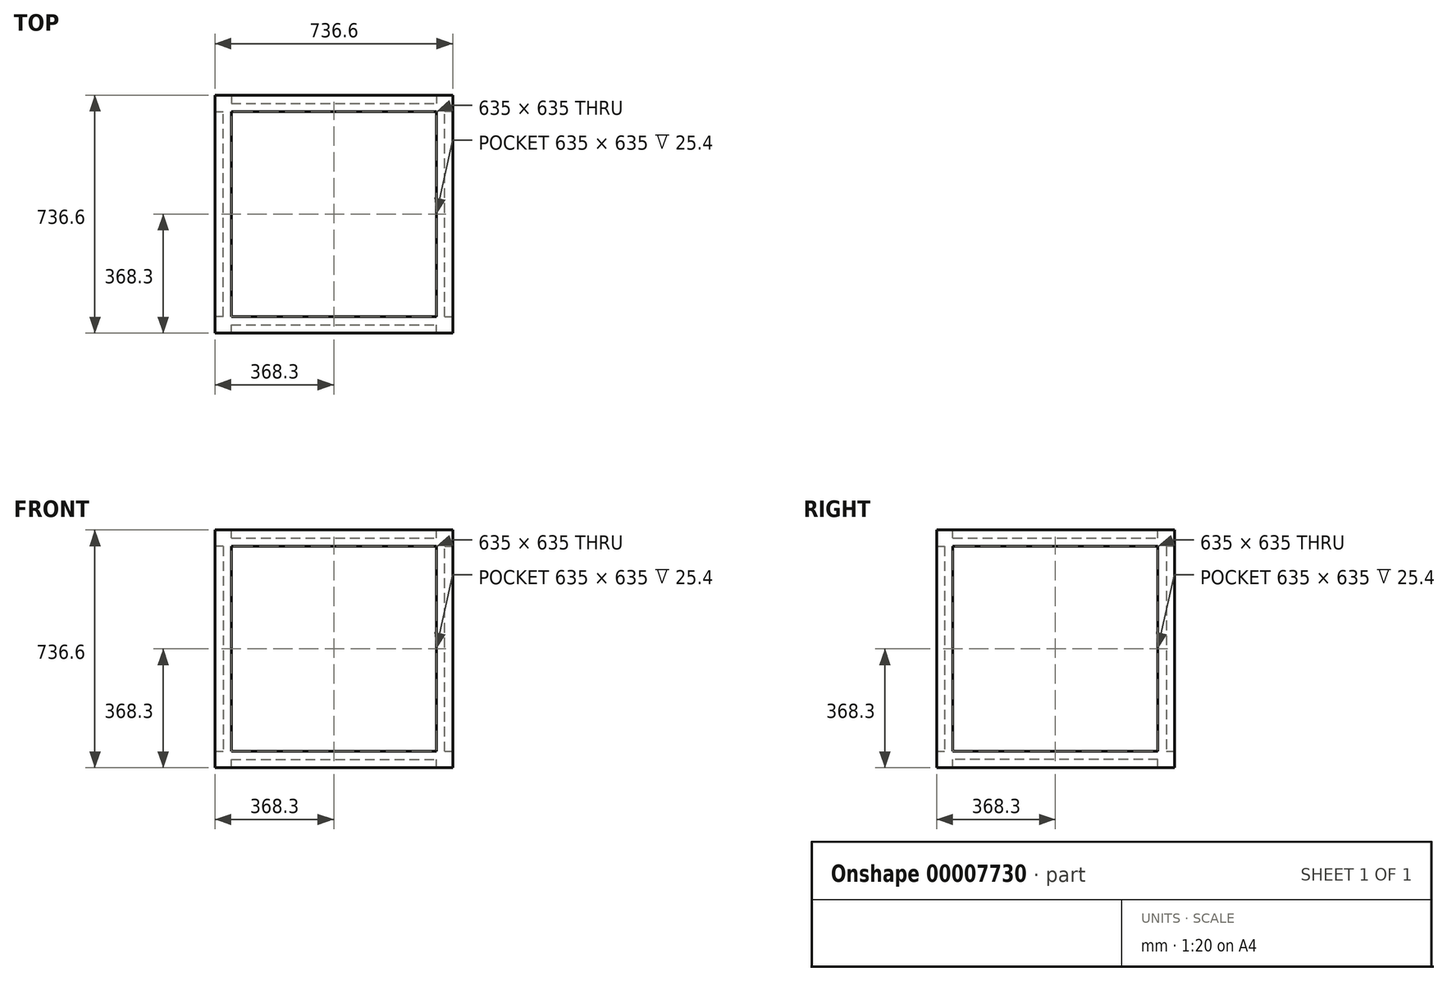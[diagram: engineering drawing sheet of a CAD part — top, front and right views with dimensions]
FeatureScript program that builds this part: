
annotation { "Feature Type Name" : "Feature", "Feature Type Description" : "" }
export const myFeature = defineFeature(function(context is Context, id is Id, definition is map)
    precondition{}
    {
        {
            var Q0;
            Q0=qCreatedBy(makeId("Front.planeOp"),FACE);
            var sketch = newSketch(context, id + "F0", { "sketchPlane" : qUnion([Q0])});
            skLineSegment(sketch, "E0.bottom", {"start": v(0, 0) * mm, "end": v(685.8, 0) * mm});
            skLineSegment(sketch, "E0.top", {"start": v(0, 685.8) * mm, "end": v(685.8, 685.8) * mm});
            skLineSegment(sketch, "E0.left", {"start": v(0, 0) * mm, "end": v(0, 685.8) * mm});
            skLineSegment(sketch, "E0.right", {"start": v(685.8, 0) * mm, "end": v(685.8, 685.8) * mm});
            skSolve(sketch);
        }
        {
            var Q0;
            Q0=makeQuery(id+"F0.imprint","IMPRINT",FACE,{"disambiguationData":[TD([[makeQuery(id+"F0.imprint","IMPRINT",EDGE,{"derivedFrom":sQuery(id+"F0.wireOp",EDGE,"E0.bottom")}),1.0]])]});
            extrude(context, id + "F1", {"entities" : qUnion([Q0]), "depth" : 685.8 * mm});
        }
        {
            var Q0;
            Q0=makeQuery(id+"F1.opExtrude","SWEPT_FACE",FACE,{"disambiguationData":[OSD([sQuery(id+"F0.wireOp",EDGE,"E0.right")])]});
            var sketch = newSketch(context, id + "F2", { "sketchPlane" : qUnion([Q0])});
            skLineSegment(sketch, "E1.0", {"start": v(-685.8, 0) * mm, "end": v(-685.8, 685.8) * mm, "construction": true});
            skLineSegment(sketch, "E2.0", {"start": v(0, 0) * mm, "end": v(0, 685.8) * mm, "construction": true});
            skLineSegment(sketch, "E3.0", {"start": v(-685.8, 685.8) * mm, "end": v(0, 685.8) * mm, "construction": true});
            skLineSegment(sketch, "E4.rect.bottom", {"start": v(-711.2, 711.2) * mm, "end": v(-660.4, 711.2) * mm});
            skLineSegment(sketch, "E4.rect.top", {"start": v(-711.2, 660.4) * mm, "end": v(-685.8, 660.4) * mm});
            skLineSegment(sketch, "E4.rect.left", {"start": v(-711.2, 711.2) * mm, "end": v(-711.2, 660.4) * mm});
            skLineSegment(sketch, "E4.rect.right", {"start": v(-660.4, 711.2) * mm, "end": v(-660.4, 685.8) * mm});
            skPoint(sketch, "E4.rect.middle", {"position": v(-685.8, 685.8) * mm});
            skPoint(sketch, "E5.orphan", {"position": v(-660.4, 660.4) * mm});
            skLineSegment(sketch, "E6", {"start": v(-660.4, 685.8) * mm, "end": v(-685.8, 685.8) * mm});
            skLineSegment(sketch, "E7", {"start": v(-685.8, 660.4) * mm, "end": v(-685.8, 685.8) * mm});
            skLineSegment(sketch, "E8.rect.bottom", {"start": v(25.4, 711.2) * mm, "end": v(-25.4, 711.2) * mm});
            skLineSegment(sketch, "E8.rect.top", {"start": v(25.4, 660.4) * mm, "end": v(0, 660.4) * mm});
            skLineSegment(sketch, "E8.rect.left", {"start": v(25.4, 711.2) * mm, "end": v(25.4, 660.4) * mm});
            skLineSegment(sketch, "E8.rect.right", {"start": v(-25.4, 711.2) * mm, "end": v(-25.4, 685.8) * mm});
            skPoint(sketch, "E8.rect.middle", {"position": v(0, 685.8) * mm});
            skLineSegment(sketch, "E9.rect.bottom", {"start": v(0, 25.4) * mm, "end": v(25.4, 25.4) * mm});
            skLineSegment(sketch, "E9.rect.top", {"start": v(-25.4, -25.4) * mm, "end": v(25.4, -25.4) * mm});
            skLineSegment(sketch, "E9.rect.right", {"start": v(25.4, 25.4) * mm, "end": v(25.4, -25.4) * mm});
            skPoint(sketch, "E9.rect.middle", {"position": v(0, 0) * mm});
            skLineSegment(sketch, "E10.rect.bottom", {"start": v(-711.2, -25.4) * mm, "end": v(-660.4, -25.4) * mm});
            skLineSegment(sketch, "E10.rect.top", {"start": v(-711.2, 25.4) * mm, "end": v(-685.8, 25.4) * mm});
            skLineSegment(sketch, "E10.rect.left", {"start": v(-711.2, -25.4) * mm, "end": v(-711.2, 25.4) * mm});
            skPoint(sketch, "E10.rect.middle", {"position": v(-685.8, 0) * mm});
            skPoint(sketch, "E11.orphan", {"position": v(-25.4, 660.4) * mm});
            skPoint(sketch, "E12.orphan", {"position": v(-660.4, 25.4) * mm});
            skPoint(sketch, "E13.orphan", {"position": v(-25.4, 25.4) * mm});
            skLineSegment(sketch, "E14", {"start": v(-25.4, 685.8) * mm, "end": v(0, 685.8) * mm});
            skLineSegment(sketch, "E15", {"start": v(0, 685.8) * mm, "end": v(0, 660.4) * mm});
            skLineSegment(sketch, "E16", {"start": v(0, 25.4) * mm, "end": v(0, 0) * mm});
            skLineSegment(sketch, "E17", {"start": v(-25.4, -25.4) * mm, "end": v(-25.4, 0) * mm});
            skLineSegment(sketch, "E18", {"start": v(-25.4, 0) * mm, "end": v(0, 0) * mm});
            skLineSegment(sketch, "E19", {"start": v(-660.4, -25.4) * mm, "end": v(-660.4, 0) * mm});
            skLineSegment(sketch, "E20", {"start": v(-660.4, 0) * mm, "end": v(-685.8, 0) * mm});
            skLineSegment(sketch, "E21", {"start": v(-685.8, 25.4) * mm, "end": v(-685.8, 0) * mm});
            skSolve(sketch);
        }
        {
            var Q0;
            Q0=makeQuery(id+"F2.imprint","IMPRINT",FACE,{"disambiguationData":[TD([[makeQuery(id+"F2.imprint","IMPRINT",EDGE,{"derivedFrom":sQuery(id+"F2.wireOp",EDGE,"E4.rect.bottom")}),-1.0]])]});
            var Q1;
            Q1=makeQuery(id+"F2.imprint","IMPRINT",FACE,{"disambiguationData":[TD([[makeQuery(id+"F2.imprint","IMPRINT",EDGE,{"derivedFrom":sQuery(id+"F2.wireOp",EDGE,"E8.rect.bottom")}),1.0]])]});
            var Q2;
            Q2=makeQuery(id+"F2.imprint","IMPRINT",FACE,{"disambiguationData":[TD([[makeQuery(id+"F2.imprint","IMPRINT",EDGE,{"derivedFrom":sQuery(id+"F2.wireOp",EDGE,"E9.rect.bottom")}),-1.0]])]});
            var Q3;
            Q3=makeQuery(id+"F2.imprint","IMPRINT",FACE,{"disambiguationData":[TD([[makeQuery(id+"F2.imprint","IMPRINT",EDGE,{"derivedFrom":sQuery(id+"F2.wireOp",EDGE,"E10.rect.bottom")}),1.0]])]});
            extrude(context, id + "F3", {"entities" : qUnion([Q0, Q1, Q2, Q3]), "operationType" : NewBodyOperationType.ADD, "oppositeDirection" : true, "depth" : 685.8 * mm});
        }
        {
            var Q0;
            Q0=makeQuery(id+"F1.opExtrude","CAP_FACE",FACE,{"disambiguationData":[OSD([sQuery(id+"F0.wireOp",EDGE,"E0.bottom"),sQuery(id+"F0.wireOp",EDGE,"E0.top"),sQuery(id+"F0.wireOp",EDGE,"E0.left"),sQuery(id+"F0.wireOp",EDGE,"E0.right")])],"isStart":true});
            var sketch = newSketch(context, id + "F4", { "sketchPlane" : qUnion([Q0])});
            skPoint(sketch, "E22.0", {"position": v(0, 685.8) * mm});
            skPoint(sketch, "E23.0", {"position": v(0, 0) * mm});
            skPoint(sketch, "E24.0", {"position": v(-685.8, 685.8) * mm});
            skPoint(sketch, "E25.0", {"position": v(-685.8, 0) * mm});
            skLineSegment(sketch, "E26.0", {"start": v(0, 711.2) * mm, "end": v(-685.8, 711.2) * mm, "construction": true});
            skLineSegment(sketch, "E27.0", {"start": v(0, -25.4) * mm, "end": v(-685.8, -25.4) * mm, "construction": true});
            skLineSegment(sketch, "E28.rect.bottom", {"start": v(-25.4, 711.2) * mm, "end": v(25.4, 711.2) * mm});
            skLineSegment(sketch, "E28.rect.top", {"start": v(-25.4, 660.4) * mm, "end": v(25.4, 660.4) * mm});
            skLineSegment(sketch, "E28.rect.left", {"start": v(-25.4, 711.2) * mm, "end": v(-25.4, 660.4) * mm});
            skLineSegment(sketch, "E28.rect.right", {"start": v(25.4, 711.2) * mm, "end": v(25.4, 660.4) * mm});
            skLineSegment(sketch, "E29.rect.bottom", {"start": v(-660.4, 711.2) * mm, "end": v(-711.2, 711.2) * mm});
            skLineSegment(sketch, "E29.rect.top", {"start": v(-660.4, 660.4) * mm, "end": v(-711.2, 660.4) * mm});
            skLineSegment(sketch, "E29.rect.left", {"start": v(-660.4, 711.2) * mm, "end": v(-660.4, 660.4) * mm});
            skLineSegment(sketch, "E29.rect.right", {"start": v(-711.2, 711.2) * mm, "end": v(-711.2, 660.4) * mm});
            skLineSegment(sketch, "E30.rect.bottom", {"start": v(-25.4, -25.4) * mm, "end": v(25.4, -25.4) * mm});
            skLineSegment(sketch, "E30.rect.top", {"start": v(-25.4, 25.4) * mm, "end": v(25.4, 25.4) * mm});
            skLineSegment(sketch, "E30.rect.left", {"start": v(-25.4, -25.4) * mm, "end": v(-25.4, 25.4) * mm});
            skLineSegment(sketch, "E30.rect.right", {"start": v(25.4, -25.4) * mm, "end": v(25.4, 25.4) * mm});
            skLineSegment(sketch, "E31.rect.bottom", {"start": v(-660.4, -25.4) * mm, "end": v(-711.2, -25.4) * mm});
            skLineSegment(sketch, "E31.rect.top", {"start": v(-660.4, 25.4) * mm, "end": v(-711.2, 25.4) * mm});
            skLineSegment(sketch, "E31.rect.left", {"start": v(-660.4, -25.4) * mm, "end": v(-660.4, 25.4) * mm});
            skLineSegment(sketch, "E31.rect.right", {"start": v(-711.2, -25.4) * mm, "end": v(-711.2, 25.4) * mm});
            skSolve(sketch);
        }
        {
            var Q0;
            Q0=makeQuery(id+"F4.imprint","IMPRINT",FACE,{"disambiguationData":[TD([[makeQuery(id+"F4.imprint","IMPRINT",EDGE,{"derivedFrom":sQuery(id+"F4.wireOp",EDGE,"E28.rect.bottom")}),-1.0]])]});
            var Q1;
            Q1=makeQuery(id+"F4.imprint","IMPRINT",FACE,{"disambiguationData":[TD([[makeQuery(id+"F4.imprint","IMPRINT",EDGE,{"derivedFrom":sQuery(id+"F4.wireOp",EDGE,"E29.rect.bottom")}),1.0]])]});
            var Q2;
            Q2=makeQuery(id+"F4.imprint","IMPRINT",FACE,{"disambiguationData":[TD([[makeQuery(id+"F4.imprint","IMPRINT",EDGE,{"derivedFrom":sQuery(id+"F4.wireOp",EDGE,"E30.rect.bottom")}),1.0]])]});
            var Q3;
            Q3=makeQuery(id+"F4.imprint","IMPRINT",FACE,{"disambiguationData":[TD([[makeQuery(id+"F4.imprint","IMPRINT",EDGE,{"derivedFrom":sQuery(id+"F4.wireOp",EDGE,"E31.rect.bottom")}),-1.0]])]});
            extrude(context, id + "F5", {"entities" : qUnion([Q0, Q1, Q2, Q3]), "operationType" : NewBodyOperationType.ADD, "oppositeDirection" : true, "depth" : 685.8 * mm});
        }
        {
            var Q0;
            {var subQ0=sQuery(id+"F4.wireOp",EDGE,"E28.rect.bottom");var subQ1=sQuery(id+"F4.wireOp",EDGE,"E29.rect.bottom");Q0=makeQuery(id+"FpNIWuuIkv2z32E_1.boolean.opBoolean","MERGE",FACE,{"derivedFrom":[makeQuery(id+"F5.boolean.opBoolean","MERGE",FACE,{"derivedFrom":[makeQuery(id+"F3.opExtrude","SWEPT_FACE",FACE,{"disambiguationData":[OSD([sQuery(id+"F2.wireOp",EDGE,"E4.rect.bottom")])]}),makeQuery(id+"F3.opExtrude","SWEPT_FACE",FACE,{"disambiguationData":[OSD([sQuery(id+"F2.wireOp",EDGE,"E8.rect.bottom")])]}),makeQuery(id+"F5.opExtrude","SWEPT_FACE",FACE,{"disambiguationData":[OSD([subQ0])]}),makeQuery(id+"F5.opExtrude","SWEPT_FACE",FACE,{"disambiguationData":[OSD([subQ1])]})]}),makeQuery(id+"FpNIWuuIkv2z32E_1.opExtrude","SWEPT_FACE",FACE,{"disambiguationData":[OSD([subQ0])]}),makeQuery(id+"FpNIWuuIkv2z32E_1.opExtrude","SWEPT_FACE",FACE,{"disambiguationData":[OSD([subQ1])]})]});}
            var sketch = newSketch(context, id + "F6", { "sketchPlane" : qUnion([Q0])});
            skLineSegment(sketch, "E32.0.0", {"start": v(25.4, -660.4) * mm, "end": v(660.4, -660.4) * mm, "construction": true});
            skLineSegment(sketch, "E32.0.1", {"start": v(660.4, -660.4) * mm, "end": v(660.4, -25.4) * mm, "construction": true});
            skLineSegment(sketch, "E32.0.2", {"start": v(660.4, -25.4) * mm, "end": v(25.4, -25.4) * mm, "construction": true});
            skLineSegment(sketch, "E33.0.0", {"start": v(711.2, -685.8) * mm, "end": v(711.2, 25.4) * mm, "construction": true});
            skLineSegment(sketch, "E33.0.1", {"start": v(711.2, 25.4) * mm, "end": v(-25.4, 25.4) * mm, "construction": true});
            skLineSegment(sketch, "E33.0.3", {"start": v(-25.4, -711.2) * mm, "end": v(609.6, -711.2) * mm, "construction": true});
            skLineSegment(sketch, "E34.bottom", {"start": v(711.2, 25.4) * mm, "end": v(660.4, 25.4) * mm, "construction": true});
            skLineSegment(sketch, "E34.top", {"start": v(711.2, -25.4) * mm, "end": v(660.4, -25.4) * mm, "construction": true});
            skLineSegment(sketch, "E34.left", {"start": v(711.2, 25.4) * mm, "end": v(711.2, -25.4) * mm, "construction": true});
            skLineSegment(sketch, "E34.right", {"start": v(660.4, 25.4) * mm, "end": v(660.4, -25.4) * mm, "construction": true});
            skLineSegment(sketch, "E35.bottom", {"start": v(711.2, 25.4) * mm, "end": v(660.4, 25.4) * mm});
            skLineSegment(sketch, "E35.top", {"start": v(711.2, -25.4) * mm, "end": v(660.4, -25.4) * mm});
            skLineSegment(sketch, "E35.left", {"start": v(711.2, 25.4) * mm, "end": v(711.2, -25.4) * mm});
            skLineSegment(sketch, "E35.right", {"start": v(660.4, 25.4) * mm, "end": v(660.4, -25.4) * mm});
            skLineSegment(sketch, "E36.bottom", {"start": v(-25.4, 25.4) * mm, "end": v(25.4, 25.4) * mm});
            skLineSegment(sketch, "E36.top", {"start": v(-25.4, -25.4) * mm, "end": v(25.4, -25.4) * mm});
            skLineSegment(sketch, "E36.left", {"start": v(-25.4, 25.4) * mm, "end": v(-25.4, -25.4) * mm});
            skLineSegment(sketch, "E36.right", {"start": v(25.4, 25.4) * mm, "end": v(25.4, -25.4) * mm});
            skLineSegment(sketch, "E37.bottom", {"start": v(25.4, -660.4) * mm, "end": v(-25.4, -660.4) * mm});
            skLineSegment(sketch, "E37.top", {"start": v(25.4, -711.2) * mm, "end": v(-25.4, -711.2) * mm});
            skLineSegment(sketch, "E37.left", {"start": v(25.4, -660.4) * mm, "end": v(25.4, -711.2) * mm});
            skLineSegment(sketch, "E37.right", {"start": v(-25.4, -660.4) * mm, "end": v(-25.4, -711.2) * mm});
            skLineSegment(sketch, "E38.bottom", {"start": v(660.4, -660.4) * mm, "end": v(711.2, -660.4) * mm});
            skLineSegment(sketch, "E38.top", {"start": v(660.4, -711.2) * mm, "end": v(711.2, -711.2) * mm});
            skLineSegment(sketch, "E38.left", {"start": v(660.4, -660.4) * mm, "end": v(660.4, -711.2) * mm});
            skLineSegment(sketch, "E38.right", {"start": v(711.2, -660.4) * mm, "end": v(711.2, -711.2) * mm});
            skSolve(sketch);
        }
        {
            var Q0;
            {var subQ6=sQuery(id+"F6.wireOp",EDGE,"E35.top");Q0=makeQuery(id+"F6.imprint","IMPRINT",FACE,{"disambiguationData":[TD([[makeQuery(id+"F6.imprint","IMPRINT",EDGE,{"derivedFrom":subQ6}),-1.0]])]});}
            var Q1;
            {var subQ1=makeQuery(id+"F3.opExtrude","CAP_EDGE",EDGE,{"disambiguationData":[OSD([sQuery(id+"F2.wireOp",EDGE,"E8.rect.bottom")])],"isStart":true});Q1=makeQuery(id+"F6.imprint","IMPRINT",FACE,{"disambiguationData":[TD([[makeQuery(id+"F6.imprint","IMPRINT",EDGE,{"derivedFrom":subQ1}),1.0]])]});}
            var Q2;
            {var subQ1=makeQuery(id+"F3.opExtrude","CAP_EDGE",EDGE,{"disambiguationData":[OSD([sQuery(id+"F2.wireOp",EDGE,"E8.rect.bottom")])],"isStart":false});Q2=makeQuery(id+"F6.imprint","IMPRINT",FACE,{"disambiguationData":[TD([[makeQuery(id+"F6.imprint","IMPRINT",EDGE,{"derivedFrom":subQ1}),-1.0]])]});}
            var Q3;
            {var subQ1=makeQuery(id+"F3.opExtrude","CAP_EDGE",EDGE,{"disambiguationData":[OSD([sQuery(id+"F2.wireOp",EDGE,"E4.rect.bottom")])],"isStart":true});Q3=makeQuery(id+"F6.imprint","IMPRINT",FACE,{"disambiguationData":[TD([[makeQuery(id+"F6.imprint","IMPRINT",EDGE,{"derivedFrom":subQ1}),-1.0]])]});}
            var Q4;
            {var subQ1=makeQuery(id+"F3.opExtrude","CAP_EDGE",EDGE,{"disambiguationData":[OSD([sQuery(id+"F2.wireOp",EDGE,"E4.rect.bottom")])],"isStart":false});Q4=makeQuery(id+"F6.imprint","IMPRINT",FACE,{"disambiguationData":[TD([[makeQuery(id+"F6.imprint","IMPRINT",EDGE,{"derivedFrom":subQ1}),1.0]])]});}
            var Q5;
            {var subQ2=sQuery(id+"F6.wireOp",EDGE,"E37.bottom");Q5=makeQuery(id+"F6.imprint","IMPRINT",FACE,{"disambiguationData":[TD([[makeQuery(id+"F6.imprint","IMPRINT",EDGE,{"derivedFrom":subQ2}),1.0]])]});}
            var Q6;
            {var subQ4=sQuery(id+"F6.wireOp",EDGE,"E38.bottom");Q6=makeQuery(id+"F6.imprint","IMPRINT",FACE,{"disambiguationData":[TD([[makeQuery(id+"F6.imprint","IMPRINT",EDGE,{"derivedFrom":subQ4}),-1.0]])]});}
            var Q7;
            {var subQ6=sQuery(id+"F6.wireOp",EDGE,"E36.top");Q7=makeQuery(id+"F6.imprint","IMPRINT",FACE,{"disambiguationData":[TD([[makeQuery(id+"F6.imprint","IMPRINT",EDGE,{"derivedFrom":subQ6}),1.0]])]});}
            extrude(context, id + "F7", {"entities" : qUnion([Q0, Q1, Q2, Q3, Q4, Q5, Q6, Q7]), "operationType" : NewBodyOperationType.ADD, "oppositeDirection" : true, "depth" : 736.6 * mm});
        }
    });
